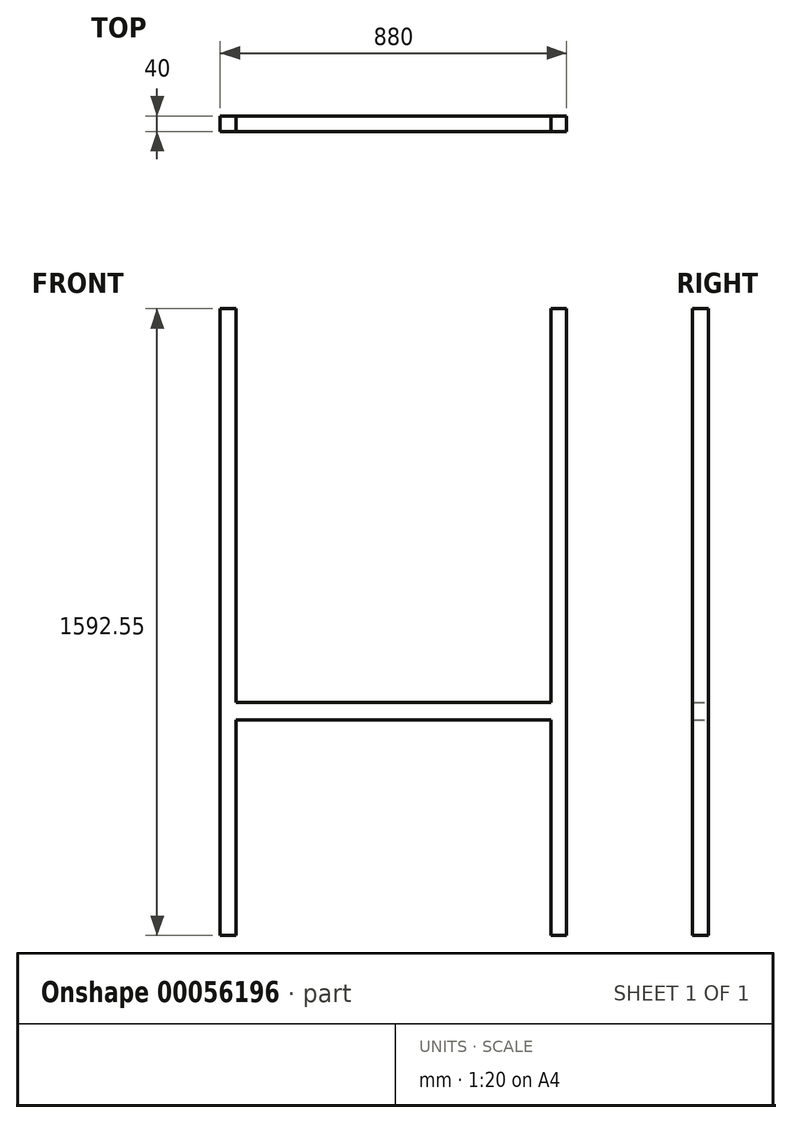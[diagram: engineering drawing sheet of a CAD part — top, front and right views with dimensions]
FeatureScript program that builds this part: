
annotation { "Feature Type Name" : "Feature", "Feature Type Description" : "" }
export const myFeature = defineFeature(function(context is Context, id is Id, definition is map)
    precondition{}
    {
        {
            var Q0;
            Q0=qCreatedBy(makeId("Front.planeOp"),FACE);
            var sketch = newSketch(context, id + "F0", { "sketchPlane" : qUnion([Q0])});
            skLineSegment(sketch, "E0", {"start": v(0, 0) * mm, "end": v(-400, 0) * mm});
            skLineSegment(sketch, "E1", {"start": v(-440, 0) * mm, "end": v(-440, -592.55) * mm});
            skLineSegment(sketch, "E2", {"start": v(-440, -592.55) * mm, "end": v(-400, -592.55) * mm});
            skLineSegment(sketch, "E3", {"start": v(-400, -592.55) * mm, "end": v(-400, -44.54) * mm});
            skLineSegment(sketch, "E4", {"start": v(-400, -44.54) * mm, "end": v(0, -44.54) * mm});
            skLineSegment(sketch, "E5", {"start": v(0, -44.54) * mm, "end": v(0, 0) * mm});
            skLineSegment(sketch, "E6", {"start": v(-440, 0) * mm, "end": v(-440, 1000) * mm});
            skLineSegment(sketch, "E7", {"start": v(-440, 1000) * mm, "end": v(-400, 1000) * mm});
            skLineSegment(sketch, "E8", {"start": v(-400, 1000) * mm, "end": v(-400, 0) * mm});
            skLineSegment(sketch, "E9.MirrorCS", {"start": v(400, -44.54) * mm, "end": v(0, -44.54) * mm});
            skLineSegment(sketch, "E10.MirrorCS", {"start": v(0, 0) * mm, "end": v(400, 0) * mm});
            skLineSegment(sketch, "E11.MirrorCS", {"start": v(400, 1000) * mm, "end": v(400, 0) * mm});
            skLineSegment(sketch, "E12.MirrorCS", {"start": v(440, 0) * mm, "end": v(440, 1000) * mm});
            skLineSegment(sketch, "E13.MirrorCS", {"start": v(440, 0) * mm, "end": v(440, -592.55) * mm});
            skLineSegment(sketch, "E14.MirrorCS", {"start": v(440, 1000) * mm, "end": v(400, 1000) * mm});
            skLineSegment(sketch, "E15.MirrorCS", {"start": v(400, -592.55) * mm, "end": v(400, -44.54) * mm});
            skLineSegment(sketch, "E16.MirrorCS", {"start": v(440, -592.55) * mm, "end": v(400, -592.55) * mm});
            skSolve(sketch);
        }
        {
            var Q0;
            Q0=makeQuery(id+"F0.imprint","IMPRINT",FACE,{"disambiguationData":[TD([[makeQuery(id+"F0.imprint","IMPRINT",EDGE,{"derivedFrom":sQuery(id+"F0.wireOp",EDGE,"E0")}),1.0]])]});
            var Q1;
            Q1=makeQuery(id+"F0.imprint","IMPRINT",FACE,{"disambiguationData":[TD([[makeQuery(id+"F0.imprint","IMPRINT",EDGE,{"derivedFrom":sQuery(id+"F0.wireOp",EDGE,"E5")}),-1.0]])]});
            extrude(context, id + "F1", {"entities" : qUnion([Q0, Q1]), "depth" : 40 * mm});
        }
    });
